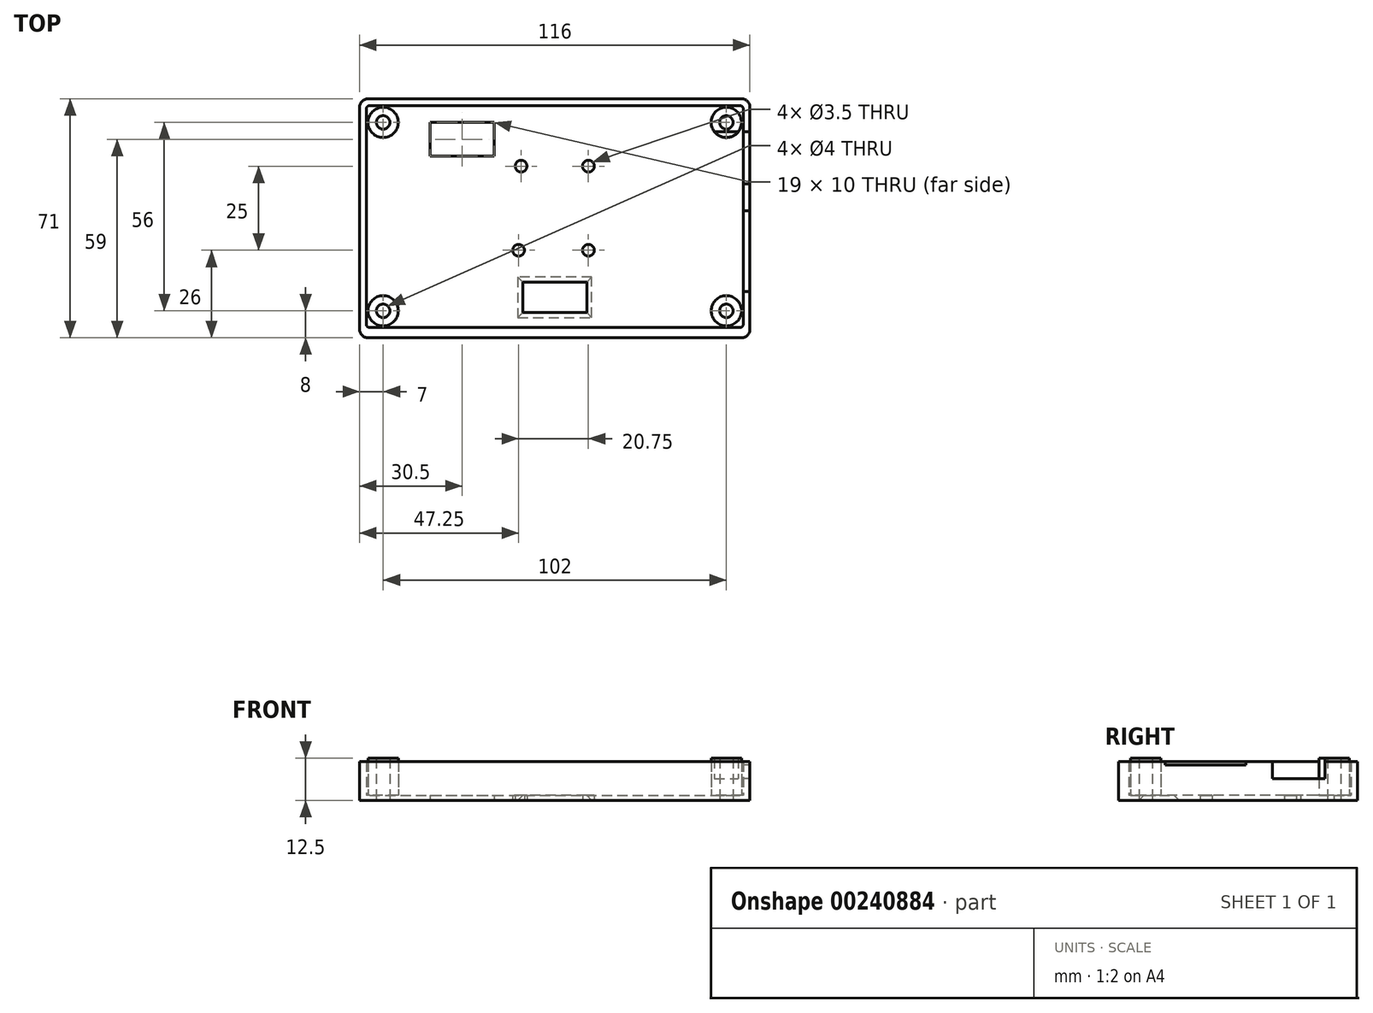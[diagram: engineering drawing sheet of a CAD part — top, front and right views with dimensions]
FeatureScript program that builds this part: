
annotation { "Feature Type Name" : "Feature", "Feature Type Description" : "" }
export const myFeature = defineFeature(function(context is Context, id is Id, definition is map)
    precondition{}
    {
        {
            var Q0;
            Q0=qCreatedBy(makeId("Top.planeOp"),FACE);
            var sketch = newSketch(context, id + "F0", { "sketchPlane" : qUnion([Q0])});
            skLineSegment(sketch, "E0.bottom", {"start": v(0, 71) * mm, "end": v(116, 71) * mm});
            skLineSegment(sketch, "E0.top", {"start": v(0, 0) * mm, "end": v(116, 0) * mm});
            skLineSegment(sketch, "E0.left", {"start": v(0, 71) * mm, "end": v(0, 0) * mm});
            skLineSegment(sketch, "E0.right", {"start": v(116, 71) * mm, "end": v(116, 0) * mm});
            skLineSegment(sketch, "E1.bottom", {"start": v(49, 8) * mm, "end": v(67, 8) * mm});
            skLineSegment(sketch, "E1.top", {"start": v(49, 16) * mm, "end": v(67, 16) * mm});
            skLineSegment(sketch, "E1.left", {"start": v(49, 16) * mm, "end": v(49, 8) * mm});
            skLineSegment(sketch, "E1.right", {"start": v(67, 16) * mm, "end": v(67, 8) * mm});
            skCircle(sketch, "E2", {"center": v(47.25, 26) * mm, "radius": 1.75 * mm});
            skCircle(sketch, "E3", {"center": v(68, 26) * mm, "radius": 1.75 * mm});
            skCircle(sketch, "E4", {"center": v(48, 51) * mm, "radius": 1.75 * mm});
            skCircle(sketch, "E5", {"center": v(68, 51) * mm, "radius": 1.75 * mm});
            skLineSegment(sketch, "E6.bottom", {"start": v(21, 64) * mm, "end": v(40, 64) * mm});
            skLineSegment(sketch, "E6.top", {"start": v(21, 54) * mm, "end": v(40, 54) * mm});
            skLineSegment(sketch, "E6.left", {"start": v(21, 64) * mm, "end": v(21, 54) * mm});
            skLineSegment(sketch, "E6.right", {"start": v(40, 64) * mm, "end": v(40, 54) * mm});
            skSolve(sketch);
        }
        {
            var Q0;
            Q0=makeQuery(id+"F0.imprint","IMPRINT",FACE,{"disambiguationData":[TD([[makeQuery(id+"F0.imprint","IMPRINT",EDGE,{"derivedFrom":sQuery(id+"F0.wireOp",EDGE,"E0.bottom")}),-1.0]])]});
            extrude(context, id + "F1", {"entities" : qUnion([Q0]), "depth" : 1.5 * mm, "offsetDistance" : 25 * mm});
        }
        {
            var Q0;
            Q0=makeQuery(id+"F1.opExtrude","CAP_FACE",FACE,{"disambiguationData":[OSD([sQuery(id+"F0.wireOp",EDGE,"E0.bottom"),sQuery(id+"F0.wireOp",EDGE,"E0.top"),sQuery(id+"F0.wireOp",EDGE,"E0.left"),sQuery(id+"F0.wireOp",EDGE,"E0.right"),sQuery(id+"F0.wireOp",EDGE,"E1.bottom"),sQuery(id+"F0.wireOp",EDGE,"E1.top"),sQuery(id+"F0.wireOp",EDGE,"E1.left"),sQuery(id+"F0.wireOp",EDGE,"E1.right")])],"isStart":false});
            var sketch = newSketch(context, id + "F2", { "sketchPlane" : qUnion([Q0])});
            skLineSegment(sketch, "E7.bottom", {"start": v(0, 71) * mm, "end": v(116, 71) * mm});
            skLineSegment(sketch, "E7.top", {"start": v(0, 0) * mm, "end": v(116, 0) * mm});
            skLineSegment(sketch, "E7.left", {"start": v(0, 71) * mm, "end": v(0, 0) * mm});
            skLineSegment(sketch, "E7.right", {"start": v(116, 71) * mm, "end": v(116, 0) * mm});
            skLineSegment(sketch, "E8.bottom", {"start": v(2, 69) * mm, "end": v(114, 69) * mm});
            skLineSegment(sketch, "E8.top", {"start": v(2, 3) * mm, "end": v(114, 3) * mm});
            skLineSegment(sketch, "E8.left", {"start": v(2, 69) * mm, "end": v(2, 3) * mm});
            skLineSegment(sketch, "E8.right", {"start": v(114, 69) * mm, "end": v(114, 3) * mm});
            skSolve(sketch);
        }
        {
            var Q0;
            Q0=qSketchRegion(id+"F2",true);
            extrude(context, id + "F3", {"entities" : qUnion([Q0]), "operationType" : NewBodyOperationType.ADD, "depth" : 10 * mm, "offsetDistance" : 25 * mm});
        }
        {
            var Q0;
            Q0=makeQuery(id+"F3.boolean.opBoolean","MERGE",EDGE,{"derivedFrom":[makeQuery(id+"F1.opExtrude","SWEPT_EDGE",EDGE,{"disambiguationData":[OSD([sQuery(id+"F0.wireOp",EDGE,"E0.top"),sQuery(id+"F0.wireOp",EDGE,"E0.left")])]}),makeQuery(id+"F3.opExtrude","SWEPT_EDGE",EDGE,{"disambiguationData":[OSD([sQuery(id+"F2.wireOp",EDGE,"E7.top"),sQuery(id+"F2.wireOp",EDGE,"E7.left")])]})]});
            var Q1;
            Q1=makeQuery(id+"F3.boolean.opBoolean","MERGE",EDGE,{"derivedFrom":[makeQuery(id+"F1.opExtrude","SWEPT_EDGE",EDGE,{"disambiguationData":[OSD([sQuery(id+"F0.wireOp",EDGE,"E0.top"),sQuery(id+"F0.wireOp",EDGE,"E0.right")])]}),makeQuery(id+"F3.opExtrude","SWEPT_EDGE",EDGE,{"disambiguationData":[OSD([sQuery(id+"F2.wireOp",EDGE,"E7.top"),sQuery(id+"F2.wireOp",EDGE,"E7.right")])]})]});
            var Q2;
            Q2=makeQuery(id+"F3.boolean.opBoolean","MERGE",EDGE,{"derivedFrom":[makeQuery(id+"F1.opExtrude","SWEPT_EDGE",EDGE,{"disambiguationData":[OSD([sQuery(id+"F0.wireOp",EDGE,"E0.bottom"),sQuery(id+"F0.wireOp",EDGE,"E0.left")])]}),makeQuery(id+"F3.opExtrude","SWEPT_EDGE",EDGE,{"disambiguationData":[OSD([sQuery(id+"F2.wireOp",EDGE,"E7.bottom"),sQuery(id+"F2.wireOp",EDGE,"E7.left")])]})]});
            var Q3;
            Q3=makeQuery(id+"F3.boolean.opBoolean","MERGE",EDGE,{"derivedFrom":[makeQuery(id+"F1.opExtrude","SWEPT_EDGE",EDGE,{"disambiguationData":[OSD([sQuery(id+"F0.wireOp",EDGE,"E0.bottom"),sQuery(id+"F0.wireOp",EDGE,"E0.right")])]}),makeQuery(id+"F3.opExtrude","SWEPT_EDGE",EDGE,{"disambiguationData":[OSD([sQuery(id+"F2.wireOp",EDGE,"E7.bottom"),sQuery(id+"F2.wireOp",EDGE,"E7.right")])]})]});
            fillet(context, id + "F4", {"entities" : qUnion([Q0, Q1, Q2, Q3]), "radius" : 2.5 * mm, "tangentPropagation" : true, "allowEdgeOverflow" : false});
        }
        {
            var Q0;
            Q0=makeQuery(id+"F3.opExtrude","SWEPT_EDGE",EDGE,{"disambiguationData":[OSD([sQuery(id+"F2.wireOp",EDGE,"E8.top"),sQuery(id+"F2.wireOp",EDGE,"E8.right")])]});
            var Q1;
            Q1=makeQuery(id+"F3.opExtrude","SWEPT_EDGE",EDGE,{"disambiguationData":[OSD([sQuery(id+"F2.wireOp",EDGE,"E8.top"),sQuery(id+"F2.wireOp",EDGE,"E8.left")])]});
            var Q2;
            Q2=makeQuery(id+"F3.opExtrude","SWEPT_EDGE",EDGE,{"disambiguationData":[OSD([sQuery(id+"F2.wireOp",EDGE,"E8.bottom"),sQuery(id+"F2.wireOp",EDGE,"E8.left")])]});
            var Q3;
            Q3=makeQuery(id+"F3.opExtrude","SWEPT_EDGE",EDGE,{"disambiguationData":[OSD([sQuery(id+"F2.wireOp",EDGE,"E8.bottom"),sQuery(id+"F2.wireOp",EDGE,"E8.right")])]});
            fillet(context, id + "F5", {"entities" : qUnion([Q0, Q1, Q2, Q3]), "radius" : 1 * mm, "tangentPropagation" : true, "allowEdgeOverflow" : false});
        }
        {
            var Q0;
            Q0=makeQuery(id+"F2.imprint","IMPRINT",FACE,{"disambiguationData":[TD([[makeQuery(id+"F2.imprint","IMPRINT",EDGE,{"derivedFrom":sQuery(id+"F2.wireOp",EDGE,"E8.bottom")}),-1.0]])]});
            var sketch = newSketch(context, id + "F6", { "sketchPlane" : qUnion([Q0])});
            skCircle(sketch, "E9", {"center": v(7, 64) * mm, "radius": 4.5 * mm});
            skCircle(sketch, "E10", {"center": v(7, 8) * mm, "radius": 4.5 * mm});
            skCircle(sketch, "E11", {"center": v(109, 8) * mm, "radius": 4.5 * mm});
            skCircle(sketch, "E12", {"center": v(109, 64) * mm, "radius": 4.5 * mm});
            skCircle(sketch, "E13", {"center": v(7, 64) * mm, "radius": 2 * mm});
            skCircle(sketch, "E14", {"center": v(7, 8) * mm, "radius": 2 * mm});
            skCircle(sketch, "E15", {"center": v(109, 64) * mm, "radius": 2 * mm});
            skCircle(sketch, "E16", {"center": v(109, 8) * mm, "radius": 2 * mm});
            skSolve(sketch);
        }
        {
            var Q0;
            Q0=qSketchRegion(id+"F6",true);
            extrude(context, id + "F7", {"entities" : qUnion([Q0]), "operationType" : NewBodyOperationType.ADD, "depth" : 11 * mm, "offsetDistance" : 25 * mm});
        }
        {
            var Q0;
            Q0=makeQuery(id+"F1.opExtrude","CAP_EDGE",EDGE,{"disambiguationData":[OSD([sQuery(id+"F0.wireOp",EDGE,"E1.right")])],"isStart":true});
            var Q1;
            Q1=makeQuery(id+"F1.opExtrude","CAP_EDGE",EDGE,{"disambiguationData":[OSD([sQuery(id+"F0.wireOp",EDGE,"E1.bottom")])],"isStart":true});
            var Q2;
            Q2=makeQuery(id+"F1.opExtrude","CAP_EDGE",EDGE,{"disambiguationData":[OSD([sQuery(id+"F0.wireOp",EDGE,"E1.left")])],"isStart":true});
            var Q3;
            Q3=makeQuery(id+"F1.opExtrude","CAP_EDGE",EDGE,{"disambiguationData":[OSD([sQuery(id+"F0.wireOp",EDGE,"E1.top")])],"isStart":true});
            chamfer(context, id + "F8", {"entities" : qUnion([Q0, Q1, Q2, Q3]), "width" : 2 * mm, "tangentPropagation" : true});
        }
        {
            var Q0;
            Q0=makeQuery(id+"F3.opExtrude","SWEPT_FACE",FACE,{"disambiguationData":[OSD([sQuery(id+"F2.wireOp",EDGE,"E8.right")])]});
            var sketch = newSketch(context, id + "F9", { "sketchPlane" : qUnion([Q0])});
            skLineSegment(sketch, "E17.bottom", {"start": v(-61.23, 15.5) * mm, "end": v(-45.73, 15.5) * mm});
            skLineSegment(sketch, "E17.top", {"start": v(-61.23, 6.5) * mm, "end": v(-45.73, 6.5) * mm});
            skLineSegment(sketch, "E17.left", {"start": v(-61.23, 15.5) * mm, "end": v(-61.23, 6.5) * mm});
            skLineSegment(sketch, "E17.right", {"start": v(-45.73, 15.5) * mm, "end": v(-45.73, 6.5) * mm});
            skLineSegment(sketch, "E18.bottom", {"start": v(-13.73, 10.5) * mm, "end": v(-37.73, 10.5) * mm});
            skLineSegment(sketch, "E18.top", {"start": v(-13.73, 15.5) * mm, "end": v(-37.73, 15.5) * mm});
            skLineSegment(sketch, "E18.left", {"start": v(-13.73, 10.5) * mm, "end": v(-13.73, 15.5) * mm});
            skLineSegment(sketch, "E18.right", {"start": v(-37.73, 10.5) * mm, "end": v(-37.73, 15.5) * mm});
            skSolve(sketch);
        }
        {
            var Q0;
            Q0=qSketchRegion(id+"F9",true);
            extrude(context, id + "F10", {"entities" : qUnion([Q0]), "operationType" : NewBodyOperationType.REMOVE, "oppositeDirection" : true, "depth" : 25 * mm});
        }
        {
            var Q0;
            Q0=makeQuery(id+"F7.boolean.opBoolean","SPLIT",FACE,{"disambiguationData":[TD([makeQuery(id+"F7.opExtrude","SWEPT_FACE",FACE,{"disambiguationData":[OSD([sQuery(id+"F6.wireOp",EDGE,"E14")])]})])],"derivedFrom":makeQuery(id+"F1.opExtrude","CAP_FACE",FACE,{"disambiguationData":[OSD([sQuery(id+"F0.wireOp",EDGE,"E0.bottom"),sQuery(id+"F0.wireOp",EDGE,"E0.top"),sQuery(id+"F0.wireOp",EDGE,"E0.left"),sQuery(id+"F0.wireOp",EDGE,"E0.right"),sQuery(id+"F0.wireOp",EDGE,"E1.bottom"),sQuery(id+"F0.wireOp",EDGE,"E1.top"),sQuery(id+"F0.wireOp",EDGE,"E1.left"),sQuery(id+"F0.wireOp",EDGE,"E1.right")])],"isStart":false})});
            var Q1;
            Q1=makeQuery(id+"F7.boolean.opBoolean","SPLIT",FACE,{"disambiguationData":[TD([makeQuery(id+"F7.opExtrude","SWEPT_FACE",FACE,{"disambiguationData":[OSD([sQuery(id+"F6.wireOp",EDGE,"E13")])]})])],"derivedFrom":makeQuery(id+"F1.opExtrude","CAP_FACE",FACE,{"disambiguationData":[OSD([sQuery(id+"F0.wireOp",EDGE,"E0.bottom"),sQuery(id+"F0.wireOp",EDGE,"E0.top"),sQuery(id+"F0.wireOp",EDGE,"E0.left"),sQuery(id+"F0.wireOp",EDGE,"E0.right"),sQuery(id+"F0.wireOp",EDGE,"E1.bottom"),sQuery(id+"F0.wireOp",EDGE,"E1.top"),sQuery(id+"F0.wireOp",EDGE,"E1.left"),sQuery(id+"F0.wireOp",EDGE,"E1.right")])],"isStart":false})});
            var Q2;
            Q2=makeQuery(id+"F7.boolean.opBoolean","SPLIT",FACE,{"disambiguationData":[TD([makeQuery(id+"F7.opExtrude","SWEPT_FACE",FACE,{"disambiguationData":[OSD([sQuery(id+"F6.wireOp",EDGE,"E16")])]})])],"derivedFrom":makeQuery(id+"F1.opExtrude","CAP_FACE",FACE,{"disambiguationData":[OSD([sQuery(id+"F0.wireOp",EDGE,"E0.bottom"),sQuery(id+"F0.wireOp",EDGE,"E0.top"),sQuery(id+"F0.wireOp",EDGE,"E0.left"),sQuery(id+"F0.wireOp",EDGE,"E0.right"),sQuery(id+"F0.wireOp",EDGE,"E1.bottom"),sQuery(id+"F0.wireOp",EDGE,"E1.top"),sQuery(id+"F0.wireOp",EDGE,"E1.left"),sQuery(id+"F0.wireOp",EDGE,"E1.right")])],"isStart":false})});
            var Q3;
            Q3=makeQuery(id+"F7.boolean.opBoolean","SPLIT",FACE,{"disambiguationData":[TD([makeQuery(id+"F7.opExtrude","SWEPT_FACE",FACE,{"disambiguationData":[OSD([sQuery(id+"F6.wireOp",EDGE,"E15")])]})])],"derivedFrom":makeQuery(id+"F1.opExtrude","CAP_FACE",FACE,{"disambiguationData":[OSD([sQuery(id+"F0.wireOp",EDGE,"E0.bottom"),sQuery(id+"F0.wireOp",EDGE,"E0.top"),sQuery(id+"F0.wireOp",EDGE,"E0.left"),sQuery(id+"F0.wireOp",EDGE,"E0.right"),sQuery(id+"F0.wireOp",EDGE,"E1.bottom"),sQuery(id+"F0.wireOp",EDGE,"E1.top"),sQuery(id+"F0.wireOp",EDGE,"E1.left"),sQuery(id+"F0.wireOp",EDGE,"E1.right")])],"isStart":false})});
            var Q4;
            Q4=sQuery(id+"F6.wireOp",EDGE,"E13");
            var Q5;
            Q5=sQuery(id+"F6.wireOp",EDGE,"E14");
            var Q6;
            Q6=sQuery(id+"F6.wireOp",EDGE,"E16");
            var Q7;
            Q7=sQuery(id+"F6.wireOp",EDGE,"E15");
            extrude(context, id + "F11", {"entities" : qUnion([Q0, Q1, Q2, Q3]), "operationType" : NewBodyOperationType.REMOVE, "surfaceEntities" : qUnion([Q4, Q5, Q6, Q7]), "oppositeDirection" : true, "depth" : 25 * mm});
        }
        {
            var Q0;
            Q0 = qSketchRegion(id + "F9", true);
            extrude(context, id + "F12", {"entities" : qUnion([Q0]), "operationType" : NewBodyOperationType.REMOVE, "depth" : 25 * mm, "offsetDistance" : 25 * mm});
        }
    });
